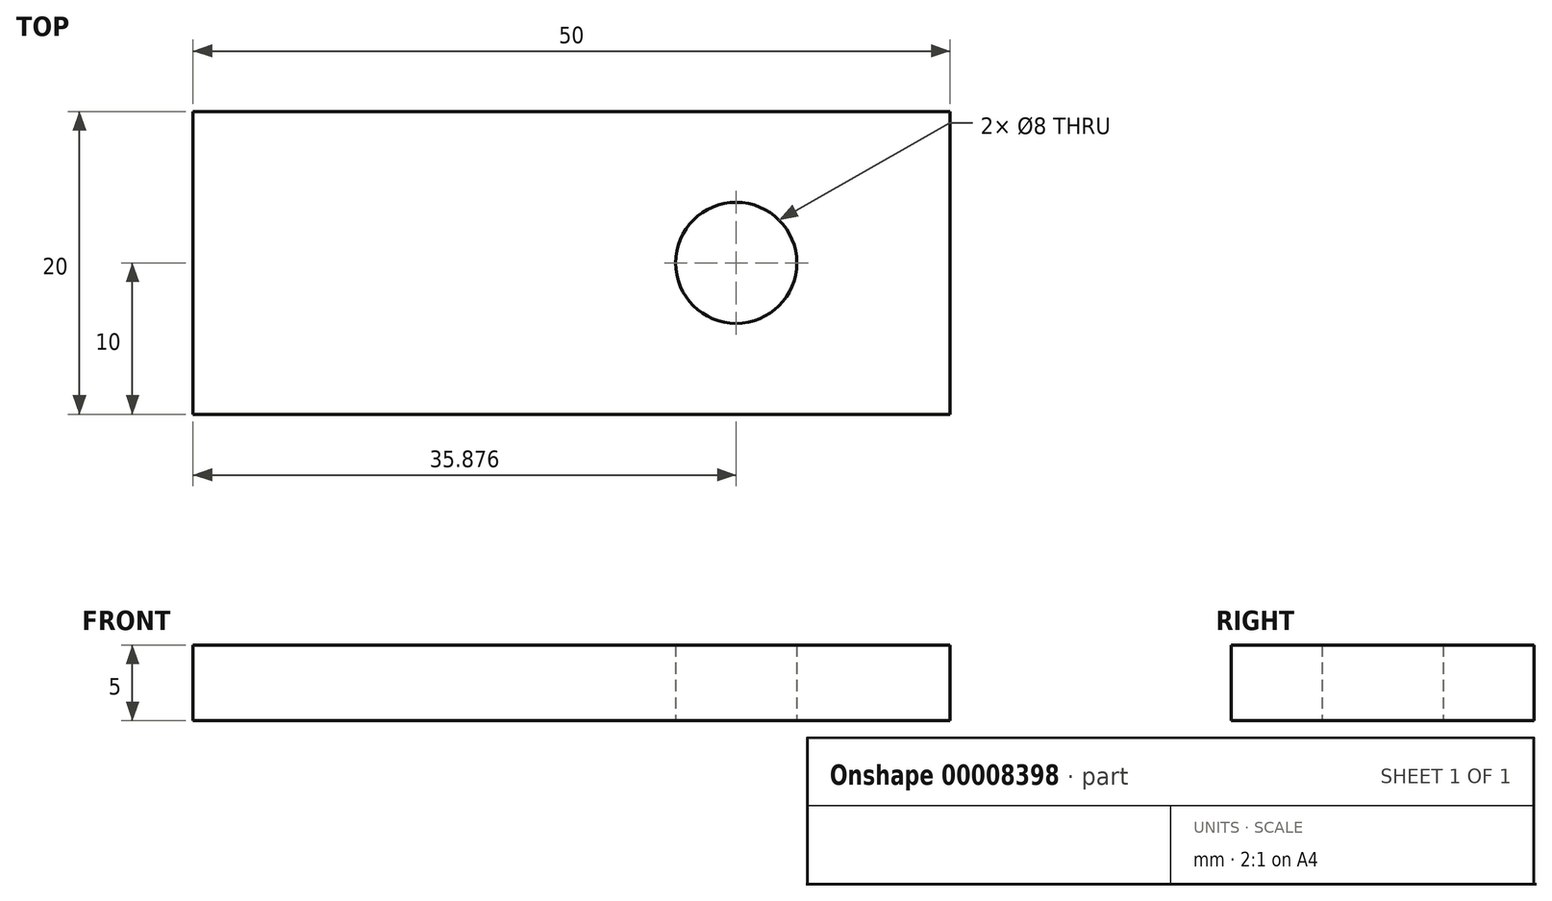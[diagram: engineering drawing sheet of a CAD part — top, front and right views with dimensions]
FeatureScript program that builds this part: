
annotation { "Feature Type Name" : "Feature", "Feature Type Description" : "" }
export const myFeature = defineFeature(function(context is Context, id is Id, definition is map)
    precondition{}
    {
        {
            var Q0;
            Q0=qCreatedBy(makeId("Top.planeOp"),FACE);
            var sketch = newSketch(context, id + "F0", { "sketchPlane" : qUnion([Q0])});
            skLineSegment(sketch, "E0.rect.bottom", {"start": v(-25, 10) * mm, "end": v(25, 10) * mm});
            skLineSegment(sketch, "E0.rect.top", {"start": v(-25, -10) * mm, "end": v(25, -10) * mm});
            skLineSegment(sketch, "E0.rect.left", {"start": v(-25, 10) * mm, "end": v(-25, -10) * mm});
            skLineSegment(sketch, "E0.rect.right", {"start": v(25, 10) * mm, "end": v(25, -10) * mm});
            skPoint(sketch, "E0.rect.middle", {"position": v(0, 0) * mm});
            skSolve(sketch);
        }
        {
            var Q0;
            Q0=makeQuery(id+"F0.imprint","IMPRINT",FACE,{"disambiguationData":[TD([[makeQuery(id+"F0.imprint","IMPRINT",EDGE,{"derivedFrom":sQuery(id+"F0.wireOp",EDGE,"E0.rect.bottom")}),-1.0]])]});
            extrude(context, id + "F1", {"entities" : qUnion([Q0]), "depth" : 5 * mm});
        }
        {
            var Q0;
            Q0=qCreatedBy(makeId("Top.planeOp"),FACE);
            var sketch = newSketch(context, id + "F2", { "sketchPlane" : qUnion([Q0])});
            skCircle(sketch, "E1", {"center": v(10.88, 0) * mm, "radius": 4 * mm});
            skSolve(sketch);
        }
        {
            var Q0;
            Q0 = qSketchRegion(id + "F2", true);
            extrude(context, id + "F3", {"entities" : qUnion([Q0]), "operationType" : NewBodyOperationType.REMOVE, "depth" : 25 * mm});
        }
    });
